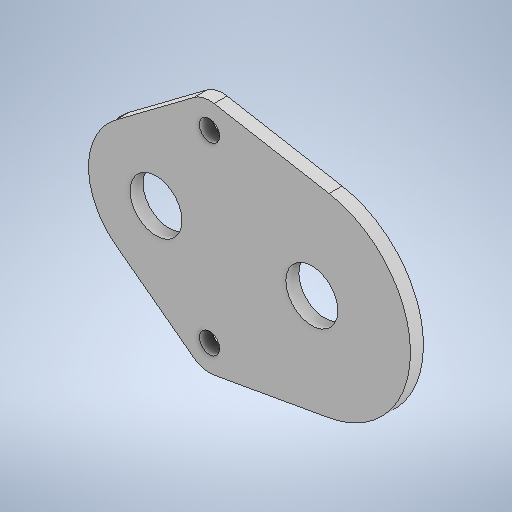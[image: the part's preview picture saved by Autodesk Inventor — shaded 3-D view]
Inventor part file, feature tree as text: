
AUTODESK INVENTOR PART (.ipt)
format: ipt  version: 2025.1 (Build 291241020, 241B)  size: 291,840 bytes
history: native  units: in
note: dims shown in document units (in); Inventor stores cm internally (conversion verified against a paired STEP export)
features: extrude x1, sketch x1
ambient origin geometry x8: Origin, YZ Plane, XZ Plane, XY Plane, X Axis, Y Axis, Z Axis, Center Point
bodies: Solid1 (feature_tree)
feature tree (2):
  extrude  "Extrusion1"  Depth=0.125in
  sketch  "Sketch1"  dims[d3=1.2in d4=1.8in d5=1.9in d6=1.3in d16=0.125in d17=0.0in d23=0.5in d30=0.5in d31=0.5in d33=0.125in d34=0.125in d35=0.196in d36=0.5in d37=0.125in d38=0.125in d39=0.196in]
